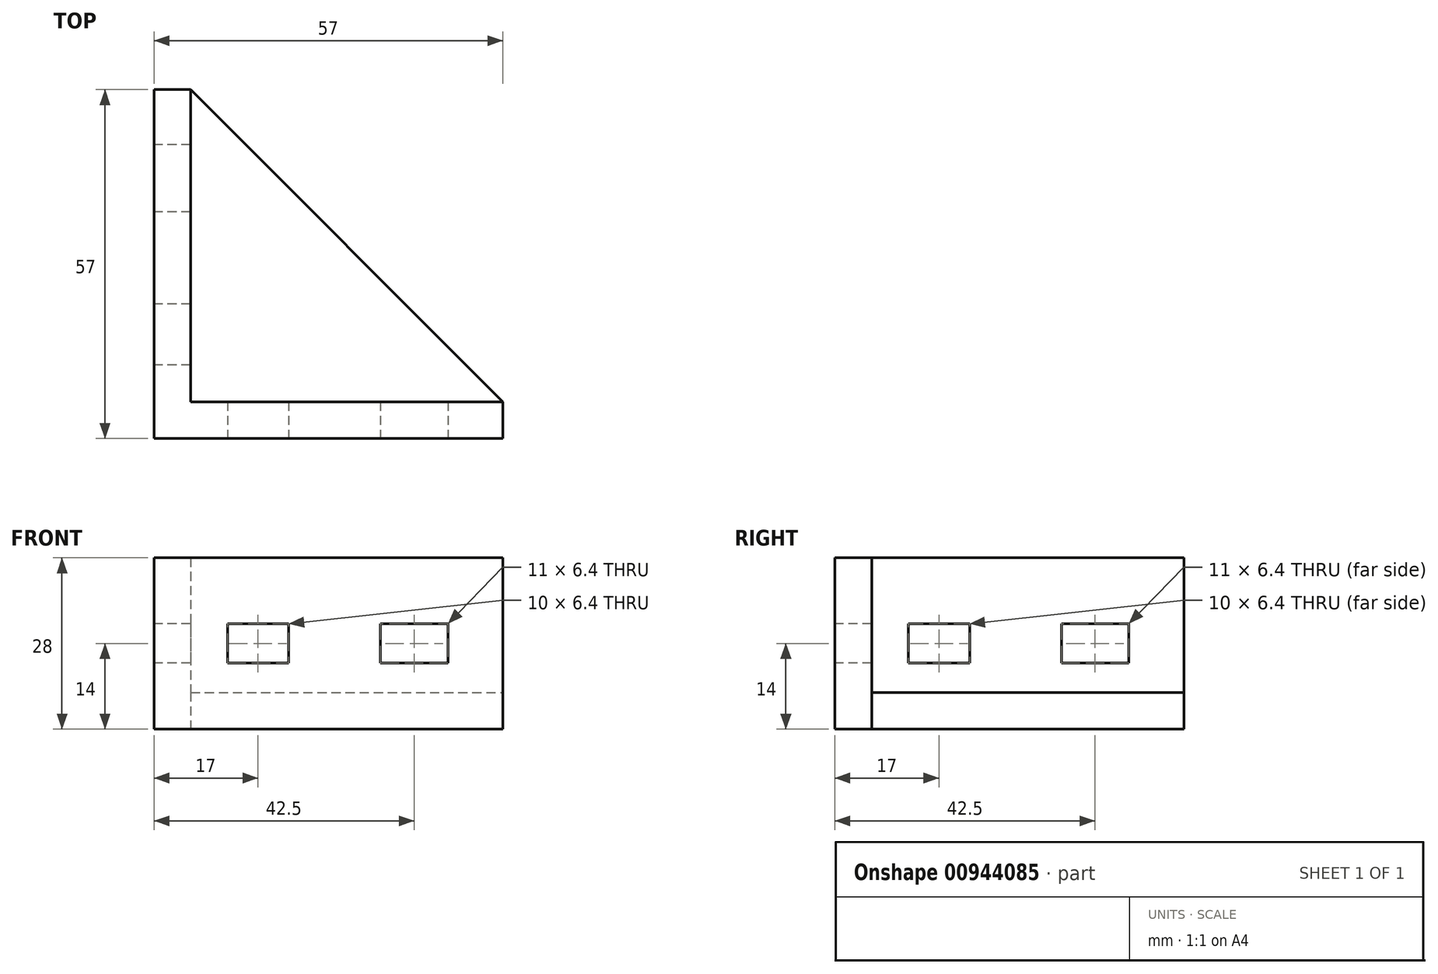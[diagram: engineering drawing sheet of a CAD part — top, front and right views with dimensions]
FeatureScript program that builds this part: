
annotation { "Feature Type Name" : "Feature", "Feature Type Description" : "" }
export const myFeature = defineFeature(function(context is Context, id is Id, definition is map)
    precondition{}
    {
        {
            var Q0;
            Q0=qCreatedBy(makeId("Top.planeOp"),FACE);
            var sketch = newSketch(context, id + "F0", { "sketchPlane" : qUnion([Q0])});
            skLineSegment(sketch, "E0", {"start": v(0, 57) * mm, "end": v(0, 0) * mm});
            skLineSegment(sketch, "E1", {"start": v(0, 0) * mm, "end": v(57, 0) * mm});
            skLineSegment(sketch, "E2", {"start": v(0, 57) * mm, "end": v(6, 57) * mm});
            skLineSegment(sketch, "E3", {"start": v(6, 57) * mm, "end": v(6, 6) * mm});
            skLineSegment(sketch, "E4", {"start": v(6, 6) * mm, "end": v(57, 6) * mm});
            skLineSegment(sketch, "E5", {"start": v(57, 6) * mm, "end": v(57, 0) * mm});
            skSolve(sketch);
        }
        {
            var Q0;
            Q0=makeQuery(id+"F0.imprint","IMPRINT",FACE,{"disambiguationData":[TD([[makeQuery(id+"F0.imprint","IMPRINT",EDGE,{"derivedFrom":sQuery(id+"F0.wireOp",EDGE,"E0")}),1.0]])]});
            extrude(context, id + "F1", {"entities" : qUnion([Q0]), "endBound" : BoundingType.SYMMETRIC, "depth" : 28 * mm, "offsetDistance" : 25 * mm});
        }
        {
            var Q0;
            Q0=makeQuery(id+"F1.opExtrude","SWEPT_FACE",FACE,{"disambiguationData":[OSD([sQuery(id+"F0.wireOp",EDGE,"E0")])]});
            var sketch = newSketch(context, id + "F2", { "sketchPlane" : qUnion([Q0])});
            skLineSegment(sketch, "E6.bottom", {"start": v(-22, -3.2) * mm, "end": v(-12, -3.2) * mm});
            skLineSegment(sketch, "E6.top", {"start": v(-22, 3.2) * mm, "end": v(-12, 3.2) * mm});
            skLineSegment(sketch, "E6.left", {"start": v(-22, -3.2) * mm, "end": v(-22, 3.2) * mm});
            skLineSegment(sketch, "E6.right", {"start": v(-12, -3.2) * mm, "end": v(-12, 3.2) * mm});
            skLineSegment(sketch, "E7.bottom", {"start": v(-48, -3.2) * mm, "end": v(-37, -3.2) * mm});
            skLineSegment(sketch, "E7.top", {"start": v(-48, 3.2) * mm, "end": v(-37, 3.2) * mm});
            skLineSegment(sketch, "E7.left", {"start": v(-48, -3.2) * mm, "end": v(-48, 3.2) * mm});
            skLineSegment(sketch, "E7.right", {"start": v(-37, -3.2) * mm, "end": v(-37, 3.2) * mm});
            skSolve(sketch);
        }
        {
            var Q0;
            Q0=makeQuery(id+"F2.imprint","IMPRINT",FACE,{"disambiguationData":[TD([[makeQuery(id+"F2.imprint","IMPRINT",EDGE,{"derivedFrom":sQuery(id+"F2.wireOp",EDGE,"E6.bottom")}),1.0]])]});
            var Q1;
            Q1=makeQuery(id+"F2.imprint","IMPRINT",FACE,{"disambiguationData":[TD([[makeQuery(id+"F2.imprint","IMPRINT",EDGE,{"derivedFrom":sQuery(id+"F2.wireOp",EDGE,"E7.bottom")}),1.0]])]});
            extrude(context, id + "F3", {"entities" : qUnion([Q0, Q1]), "operationType" : NewBodyOperationType.REMOVE, "oppositeDirection" : true, "depth" : 25 * mm, "offsetDistance" : 25 * mm});
        }
        {
            var Q0;
            Q0=makeQuery(id+"F1.opExtrude","CAP_FACE",FACE,{"disambiguationData":[OSD([sQuery(id+"F0.wireOp",EDGE,"E0"),sQuery(id+"F0.wireOp",EDGE,"E1"),sQuery(id+"F0.wireOp",EDGE,"E2"),sQuery(id+"F0.wireOp",EDGE,"E3"),sQuery(id+"F0.wireOp",EDGE,"E4"),sQuery(id+"F0.wireOp",EDGE,"E5")])],"isStart":true});
            var sketch = newSketch(context, id + "F4", { "sketchPlane" : qUnion([Q0])});
            skLineSegment(sketch, "E8", {"start": v(57, -6) * mm, "end": v(6, -57) * mm});
            skSolve(sketch);
        }
        {
            var Q0;
            Q0=makeQuery(id+"F4.imprint","IMPRINT",FACE,{"disambiguationData":[TD([[makeQuery(id+"F4.imprint","IMPRINT",EDGE,{"derivedFrom":sQuery(id+"F4.wireOp",EDGE,"E8")}),-1.0]])]});
            extrude(context, id + "F5", {"entities" : qUnion([Q0]), "operationType" : NewBodyOperationType.ADD, "oppositeDirection" : true, "depth" : 6 * mm, "offsetDistance" : 25 * mm});
        }
        {
            var Q0;
            Q0=makeQuery(id+"F1.opExtrude","SWEPT_FACE",FACE,{"disambiguationData":[OSD([sQuery(id+"F0.wireOp",EDGE,"E1")])]});
            var sketch = newSketch(context, id + "F6", { "sketchPlane" : qUnion([Q0])});
            skLineSegment(sketch, "E9.bottom", {"start": v(12, 3.2) * mm, "end": v(22, 3.2) * mm});
            skLineSegment(sketch, "E9.top", {"start": v(12, -3.2) * mm, "end": v(22, -3.2) * mm});
            skLineSegment(sketch, "E9.left", {"start": v(12, 3.2) * mm, "end": v(12, -3.2) * mm});
            skLineSegment(sketch, "E9.right", {"start": v(22, 3.2) * mm, "end": v(22, -3.2) * mm});
            skLineSegment(sketch, "E10.bottom", {"start": v(37, 3.2) * mm, "end": v(48, 3.2) * mm});
            skLineSegment(sketch, "E10.top", {"start": v(37, -3.2) * mm, "end": v(48, -3.2) * mm});
            skLineSegment(sketch, "E10.left", {"start": v(37, 3.2) * mm, "end": v(37, -3.2) * mm});
            skLineSegment(sketch, "E10.right", {"start": v(48, 3.2) * mm, "end": v(48, -3.2) * mm});
            skSolve(sketch);
        }
        {
            var Q0;
            Q0=makeQuery(id+"F6.imprint","IMPRINT",FACE,{"disambiguationData":[TD([[makeQuery(id+"F6.imprint","IMPRINT",EDGE,{"derivedFrom":sQuery(id+"F6.wireOp",EDGE,"E9.bottom")}),-1.0]])]});
            var Q1;
            Q1=makeQuery(id+"F6.imprint","IMPRINT",FACE,{"disambiguationData":[TD([[makeQuery(id+"F6.imprint","IMPRINT",EDGE,{"derivedFrom":sQuery(id+"F6.wireOp",EDGE,"E10.bottom")}),-1.0]])]});
            extrude(context, id + "F7", {"entities" : qUnion([Q0, Q1]), "operationType" : NewBodyOperationType.REMOVE, "oppositeDirection" : true, "depth" : 25 * mm, "offsetDistance" : 25 * mm});
        }
        {
            var Q0;
            Q0=makeQuery(id+"F1.opExtrude","SWEPT_FACE",FACE,{"disambiguationData":[OSD([sQuery(id+"F0.wireOp",EDGE,"E1")])]});
            var sketch = newSketch(context, id + "F8", { "sketchPlane" : qUnion([Q0])});
            skLineSegment(sketch, "E11", {"start": v(0, 0) * mm, "end": v(30, 0) * mm, "construction": true});
            skSolve(sketch);
        }
    });
